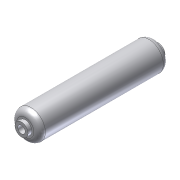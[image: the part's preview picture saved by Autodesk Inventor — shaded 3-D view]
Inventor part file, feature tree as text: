
AUTODESK INVENTOR PART (.ipt)
format: ipt  version: 2012 (Build 160160000, 160)  size: 119,296 bytes
history: native  units: in
note: dims shown in document units (in); Inventor stores cm internally (conversion verified against a paired STEP export)
features: extrude x3, sketch x3, fillet x1, shell x1
ambient origin geometry x8: Origin, YZ Plane, XZ Plane, XY Plane, X Axis, Y Axis, Z Axis, Center Point
bodies: Solid1 (feature_tree)
feature tree (8):
  extrude  "Extrusion1"  Depth=11.261in TaperAngle=0.0deg
  extrude  "Extrusion2"  Depth=0.329in TaperAngle=0.0deg
  extrude  "Extrusion3"  Depth=0.329in TaperAngle=0.0deg
  fillet  "Fillet1"  Radius=0.5in
  shell  "Shell1"  Thickness=0.25in
  sketch  "Sketch1"  dims[d0=2.5in d1=11.261in d2=0.0in]
  sketch  "Sketch2"  dims[d3=1.142in d4=0.329in d5=0.0in]
  sketch  "Sketch3"  dims[d6=1.142in d7=0.329in d8=0.0in d9=0.5in d10=0.25in]
